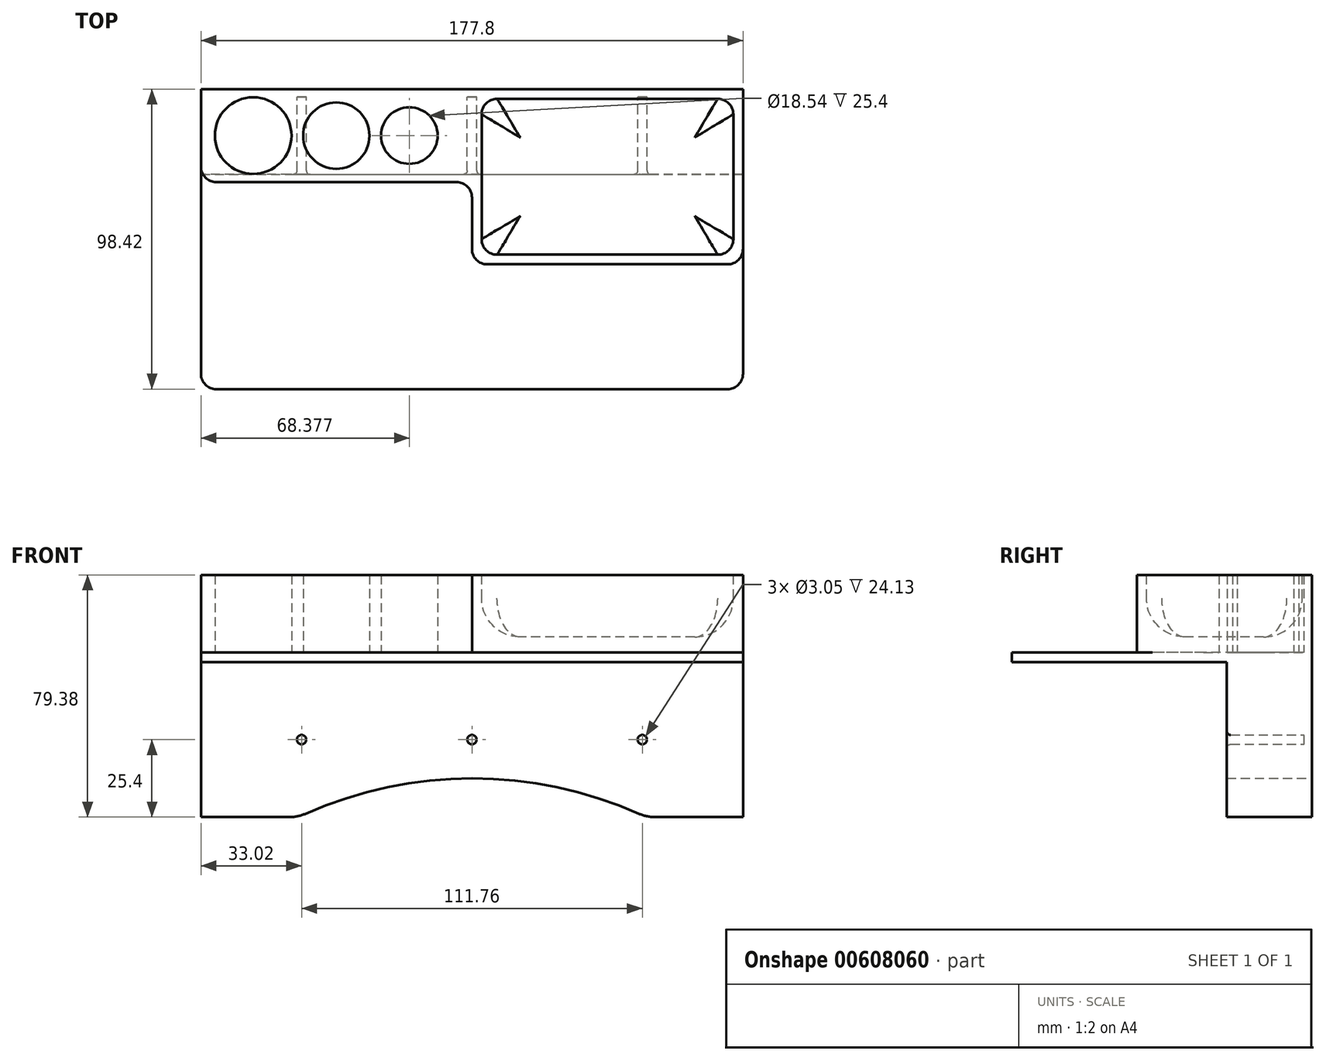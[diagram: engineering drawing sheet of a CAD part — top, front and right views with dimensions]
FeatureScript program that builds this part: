
annotation { "Feature Type Name" : "Feature", "Feature Type Description" : "" }
export const myFeature = defineFeature(function(context is Context, id is Id, definition is map)
    precondition{}
    {
        {
            var Q0;
            Q0=qCreatedBy(makeId("Top.planeOp"),FACE);
            var sketch = newSketch(context, id + "F0", { "sketchPlane" : qUnion([Q0])});
            skLineSegment(sketch, "E0.bottom", {"start": v(88.9, 47.62) * mm, "end": v(-88.9, 47.62) * mm});
            skLineSegment(sketch, "E0.top", {"start": v(88.9, -47.63) * mm, "end": v(-88.9, -47.63) * mm});
            skLineSegment(sketch, "E0.left", {"start": v(88.9, 47.62) * mm, "end": v(88.9, -47.63) * mm});
            skLineSegment(sketch, "E0.right", {"start": v(-88.9, 47.62) * mm, "end": v(-88.9, -47.63) * mm});
            skPoint(sketch, "E0.middle", {"position": v(0, 0) * mm});
            skLineSegment(sketch, "E1", {"start": v(-88.9, 47.62) * mm, "end": v(-88.9, 50.8) * mm});
            skLineSegment(sketch, "E2", {"start": v(-88.9, 50.8) * mm, "end": v(88.9, 50.8) * mm});
            skLineSegment(sketch, "E3", {"start": v(88.9, 50.8) * mm, "end": v(88.9, 47.62) * mm});
            skSolve(sketch);
        }
        {
            var Q0;
            Q0=makeQuery(id+"F0.imprint","IMPRINT",FACE,{"disambiguationData":[TD([[makeQuery(id+"F0.imprint","IMPRINT",EDGE,{"derivedFrom":sQuery(id+"F0.wireOp",EDGE,"E0.bottom")}),1.0]])]});
            var Q1;
            Q1=makeQuery(id+"F0.imprint","IMPRINT",FACE,{"disambiguationData":[TD([[makeQuery(id+"F0.imprint","IMPRINT",EDGE,{"derivedFrom":sQuery(id+"F0.wireOp",EDGE,"E0.bottom")}),-1.0]])]});
            extrude(context, id + "F1", {"entities" : qUnion([Q0, Q1]), "depth" : 3.17 * mm, "offsetDistance" : 25.4 * mm});
        }
        {
            var Q0;
            Q0=makeQuery(id+"F1.opExtrude","SWEPT_EDGE",EDGE,{"disambiguationData":[OSD([sQuery(id+"F0.wireOp",EDGE,"E0.top"),sQuery(id+"F0.wireOp",EDGE,"E0.right")])]});
            var Q1;
            Q1=makeQuery(id+"F1.opExtrude","SWEPT_EDGE",EDGE,{"disambiguationData":[OSD([sQuery(id+"F0.wireOp",EDGE,"E0.top"),sQuery(id+"F0.wireOp",EDGE,"E0.left")])]});
            fillet(context, id + "F2", {"entities" : qUnion([Q0, Q1]), "radius" : 5.08 * mm, "tangentPropagation" : true, "allowEdgeOverflow" : false});
        }
        {
            var Q0;
            Q0=makeQuery(id+"F1.opExtrude","CAP_FACE",FACE,{"disambiguationData":[OSD([sQuery(id+"F0.wireOp",EDGE,"E0.bottom"),sQuery(id+"F0.wireOp",EDGE,"E0.top"),sQuery(id+"F0.wireOp",EDGE,"E0.left"),sQuery(id+"F0.wireOp",EDGE,"E0.right")])],"isStart":false});
            var sketch = newSketch(context, id + "F3", { "sketchPlane" : qUnion([Q0])});
            skLineSegment(sketch, "E4.0", {"start": v(88.9, 47.62) * mm, "end": v(-88.9, 47.62) * mm});
            skLineSegment(sketch, "E5.0", {"start": v(88.9, 50.8) * mm, "end": v(-88.9, 50.8) * mm});
            skLineSegment(sketch, "E6.0", {"start": v(88.9, -3.18) * mm, "end": v(-88.9, -3.18) * mm});
            skLineSegment(sketch, "E7.0", {"start": v(88.9, -6.69) * mm, "end": v(-88.9, -6.69) * mm});
            skLineSegment(sketch, "E8", {"start": v(88.9, 50.8) * mm, "end": v(88.9, -6.69) * mm});
            skLineSegment(sketch, "E9", {"start": v(-88.9, 50.8) * mm, "end": v(-88.9, -6.69) * mm});
            skLineSegment(sketch, "E10", {"start": v(-88.9, 35.56) * mm, "end": v(88.9, 35.56) * mm});
            skCircle(sketch, "E11", {"center": v(-71.76, 35.56) * mm, "radius": 12.57 * mm});
            skCircle(sketch, "E12", {"center": v(-44.49, 35.56) * mm, "radius": 10.88 * mm});
            skCircle(sketch, "E13", {"center": v(-20.52, 35.56) * mm, "radius": 9.27 * mm});
            skLineSegment(sketch, "E14.0", {"start": v(-88.9, 20.32) * mm, "end": v(88.9, 20.32) * mm});
            skLineSegment(sketch, "E15", {"start": v(0, 50.8) * mm, "end": v(0, -6.69) * mm});
            skLineSegment(sketch, "E16.0", {"start": v(3.18, 50.8) * mm, "end": v(3.18, -6.69) * mm});
            skLineSegment(sketch, "E17.0", {"start": v(85.73, 50.8) * mm, "end": v(85.73, -6.69) * mm});
            skSolve(sketch);
        }
        {
            var Q0;
            {var subQ0=sQuery(id+"F3.wireOp",EDGE,"E9");var subQ1=sQuery(id+"F3.wireOp",EDGE,"E4.0");var subQ2=makeQuery(id+"F3.imprint","INTERSECT",VERTEX,{"derivedFrom":[subQ1,subQ0]});Q0=makeQuery(id+"F3.imprint","IMPRINT",FACE,{"disambiguationData":[TD([[makeQuery(id+"F3.imprint","IMPRINT",EDGE,{"disambiguationData":[TD([[subQ2,1.0]])],"derivedFrom":subQ1}),1.0]])]});}
            var Q1;
            {var subQ1=sQuery(id+"F3.wireOp",EDGE,"E4.0");var subQ5=sQuery(id+"F3.wireOp",EDGE,"E15");var subQ9=makeQuery(id+"F3.imprint","INTERSECT",VERTEX,{"derivedFrom":[subQ1,subQ5]});Q1=makeQuery(id+"F3.imprint","IMPRINT",FACE,{"disambiguationData":[TD([[makeQuery(id+"F3.imprint","IMPRINT",EDGE,{"disambiguationData":[TD([[subQ9,-1.0]])],"derivedFrom":subQ1}),-1.0]])]});}
            var Q2;
            {var subQ3=sQuery(id+"F3.wireOp",EDGE,"E15");var subQ11=sQuery(id+"F3.wireOp",EDGE,"E4.0");var subQ12=makeQuery(id+"F3.imprint","INTERSECT",VERTEX,{"derivedFrom":[subQ11,subQ3]});Q2=makeQuery(id+"F3.imprint","IMPRINT",FACE,{"disambiguationData":[TD([[makeQuery(id+"F3.imprint","IMPRINT",EDGE,{"disambiguationData":[TD([[subQ12,-1.0]])],"derivedFrom":subQ11}),1.0]])]});}
            var Q3;
            {var subQ1=sQuery(id+"F3.wireOp",EDGE,"E10");var subQ13=sQuery(id+"F3.wireOp",EDGE,"E9");var subQ14=makeQuery(id+"F3.imprint","INTERSECT",VERTEX,{"derivedFrom":[subQ13,subQ1]});Q3=makeQuery(id+"F3.imprint","IMPRINT",FACE,{"disambiguationData":[TD([[makeQuery(id+"F3.imprint","IMPRINT",EDGE,{"disambiguationData":[TD([[subQ14,-1.0]])],"derivedFrom":subQ13}),1.0]])]});}
            var Q4;
            {var subQ0=sQuery(id+"F3.wireOp",EDGE,"E16.0");var subQ1=sQuery(id+"F3.wireOp",EDGE,"E4.0");var subQ2=makeQuery(id+"F3.imprint","INTERSECT",VERTEX,{"derivedFrom":[subQ1,subQ0]});Q4=makeQuery(id+"F3.imprint","IMPRINT",FACE,{"disambiguationData":[TD([[makeQuery(id+"F3.imprint","IMPRINT",EDGE,{"disambiguationData":[TD([[subQ2,-1.0]])],"derivedFrom":subQ1}),-1.0]])]});}
            var Q5;
            {var subQ0=sQuery(id+"F3.wireOp",EDGE,"E16.0");var subQ1=sQuery(id+"F3.wireOp",EDGE,"E4.0");var subQ2=makeQuery(id+"F3.imprint","INTERSECT",VERTEX,{"derivedFrom":[subQ1,subQ0]});Q5=makeQuery(id+"F3.imprint","IMPRINT",FACE,{"disambiguationData":[TD([[makeQuery(id+"F3.imprint","IMPRINT",EDGE,{"disambiguationData":[TD([[subQ2,-1.0]])],"derivedFrom":subQ1}),1.0]])]});}
            var Q6;
            {var subQ0=sQuery(id+"F3.wireOp",EDGE,"E15");var subQ1=sQuery(id+"F3.wireOp",EDGE,"E10");var subQ2=makeQuery(id+"F3.imprint","INTERSECT",VERTEX,{"derivedFrom":[subQ1,subQ0]});Q6=makeQuery(id+"F3.imprint","IMPRINT",FACE,{"disambiguationData":[TD([[makeQuery(id+"F3.imprint","IMPRINT",EDGE,{"disambiguationData":[TD([[subQ2,-1.0]])],"derivedFrom":subQ1}),-1.0]])]});}
            var Q7;
            {var subQ0=sQuery(id+"F3.wireOp",EDGE,"E17.0");var subQ1=sQuery(id+"F3.wireOp",EDGE,"E4.0");var subQ2=makeQuery(id+"F3.imprint","INTERSECT",VERTEX,{"derivedFrom":[subQ1,subQ0]});Q7=makeQuery(id+"F3.imprint","IMPRINT",FACE,{"disambiguationData":[TD([[makeQuery(id+"F3.imprint","IMPRINT",EDGE,{"disambiguationData":[TD([[subQ2,-1.0]])],"derivedFrom":subQ1}),-1.0]])]});}
            var Q8;
            {var subQ0=sQuery(id+"F3.wireOp",EDGE,"E8");var subQ1=sQuery(id+"F3.wireOp",EDGE,"E4.0");var subQ2=makeQuery(id+"F3.imprint","INTERSECT",VERTEX,{"derivedFrom":[subQ1,subQ0]});Q8=makeQuery(id+"F3.imprint","IMPRINT",FACE,{"disambiguationData":[TD([[makeQuery(id+"F3.imprint","IMPRINT",EDGE,{"disambiguationData":[TD([[subQ2,-1.0]])],"derivedFrom":subQ1}),-1.0]])]});}
            var Q9;
            {var subQ0=sQuery(id+"F3.wireOp",EDGE,"E8");var subQ1=sQuery(id+"F3.wireOp",EDGE,"E4.0");var subQ2=makeQuery(id+"F3.imprint","INTERSECT",VERTEX,{"derivedFrom":[subQ1,subQ0]});Q9=makeQuery(id+"F3.imprint","IMPRINT",FACE,{"disambiguationData":[TD([[makeQuery(id+"F3.imprint","IMPRINT",EDGE,{"disambiguationData":[TD([[subQ2,-1.0]])],"derivedFrom":subQ1}),1.0]])]});}
            var Q10;
            {var subQ0=sQuery(id+"F3.wireOp",EDGE,"E10");var subQ1=sQuery(id+"F3.wireOp",EDGE,"E8");var subQ2=makeQuery(id+"F3.imprint","INTERSECT",VERTEX,{"derivedFrom":[subQ1,subQ0]});Q10=makeQuery(id+"F3.imprint","IMPRINT",FACE,{"disambiguationData":[TD([[makeQuery(id+"F3.imprint","IMPRINT",EDGE,{"disambiguationData":[TD([[subQ2,-1.0]])],"derivedFrom":subQ1}),-1.0]])]});}
            var Q11;
            {var subQ0=sQuery(id+"F3.wireOp",EDGE,"E17.0");var subQ1=sQuery(id+"F3.wireOp",EDGE,"E4.0");var subQ2=makeQuery(id+"F3.imprint","INTERSECT",VERTEX,{"derivedFrom":[subQ1,subQ0]});Q11=makeQuery(id+"F3.imprint","IMPRINT",FACE,{"disambiguationData":[TD([[makeQuery(id+"F3.imprint","IMPRINT",EDGE,{"disambiguationData":[TD([[subQ2,-1.0]])],"derivedFrom":subQ1}),1.0]])]});}
            var Q12;
            {var subQ0=sQuery(id+"F3.wireOp",EDGE,"E16.0");var subQ1=sQuery(id+"F3.wireOp",EDGE,"E10");var subQ2=makeQuery(id+"F3.imprint","INTERSECT",VERTEX,{"derivedFrom":[subQ1,subQ0]});Q12=makeQuery(id+"F3.imprint","IMPRINT",FACE,{"disambiguationData":[TD([[makeQuery(id+"F3.imprint","IMPRINT",EDGE,{"disambiguationData":[TD([[subQ2,-1.0]])],"derivedFrom":subQ1}),-1.0]])]});}
            var Q13;
            {var subQ0=sQuery(id+"F3.wireOp",EDGE,"E17.0");var subQ1=sQuery(id+"F3.wireOp",EDGE,"E6.0");var subQ2=makeQuery(id+"F3.imprint","INTERSECT",VERTEX,{"derivedFrom":[subQ1,subQ0]});Q13=makeQuery(id+"F3.imprint","IMPRINT",FACE,{"disambiguationData":[TD([[makeQuery(id+"F3.imprint","IMPRINT",EDGE,{"disambiguationData":[TD([[subQ2,-1.0]])],"derivedFrom":subQ1}),-1.0]])]});}
            var Q14;
            {var subQ0=sQuery(id+"F3.wireOp",EDGE,"E16.0");var subQ1=sQuery(id+"F3.wireOp",EDGE,"E6.0");var subQ2=makeQuery(id+"F3.imprint","INTERSECT",VERTEX,{"derivedFrom":[subQ1,subQ0]});Q14=makeQuery(id+"F3.imprint","IMPRINT",FACE,{"disambiguationData":[TD([[makeQuery(id+"F3.imprint","IMPRINT",EDGE,{"disambiguationData":[TD([[subQ2,-1.0]])],"derivedFrom":subQ1}),1.0]])]});}
            var Q15;
            {var subQ0=sQuery(id+"F3.wireOp",EDGE,"E17.0");var subQ1=sQuery(id+"F3.wireOp",EDGE,"E6.0");var subQ2=makeQuery(id+"F3.imprint","INTERSECT",VERTEX,{"derivedFrom":[subQ1,subQ0]});Q15=makeQuery(id+"F3.imprint","IMPRINT",FACE,{"disambiguationData":[TD([[makeQuery(id+"F3.imprint","IMPRINT",EDGE,{"disambiguationData":[TD([[subQ2,-1.0]])],"derivedFrom":subQ1}),1.0]])]});}
            var Q16;
            {var subQ0=sQuery(id+"F3.wireOp",EDGE,"E8");var subQ1=sQuery(id+"F3.wireOp",EDGE,"E6.0");var subQ2=makeQuery(id+"F3.imprint","INTERSECT",VERTEX,{"derivedFrom":[subQ1,subQ0]});Q16=makeQuery(id+"F3.imprint","IMPRINT",FACE,{"disambiguationData":[TD([[makeQuery(id+"F3.imprint","IMPRINT",EDGE,{"disambiguationData":[TD([[subQ2,-1.0]])],"derivedFrom":subQ1}),-1.0]])]});}
            var Q17;
            {var subQ0=sQuery(id+"F3.wireOp",EDGE,"E8");var subQ1=sQuery(id+"F3.wireOp",EDGE,"E6.0");var subQ2=makeQuery(id+"F3.imprint","INTERSECT",VERTEX,{"derivedFrom":[subQ1,subQ0]});Q17=makeQuery(id+"F3.imprint","IMPRINT",FACE,{"disambiguationData":[TD([[makeQuery(id+"F3.imprint","IMPRINT",EDGE,{"disambiguationData":[TD([[subQ2,-1.0]])],"derivedFrom":subQ1}),1.0]])]});}
            var Q18;
            {var subQ0=sQuery(id+"F3.wireOp",EDGE,"E16.0");var subQ1=sQuery(id+"F3.wireOp",EDGE,"E6.0");var subQ2=makeQuery(id+"F3.imprint","INTERSECT",VERTEX,{"derivedFrom":[subQ1,subQ0]});Q18=makeQuery(id+"F3.imprint","IMPRINT",FACE,{"disambiguationData":[TD([[makeQuery(id+"F3.imprint","IMPRINT",EDGE,{"disambiguationData":[TD([[subQ2,-1.0]])],"derivedFrom":subQ1}),-1.0]])]});}
            extrude(context, id + "F4", {"entities" : qUnion([Q0, Q1, Q2, Q3, Q4, Q5, Q6, Q7, Q8, Q9, Q10, Q11, Q12, Q13, Q14, Q15, Q16, Q17, Q18]), "operationType" : NewBodyOperationType.ADD, "depth" : 25.4 * mm, "offsetDistance" : 25.4 * mm});
        }
        {
            var Q0;
            Q0=makeQuery(id+"F4.opExtrude","CAP_FACE",FACE,{"disambiguationData":[OSD([sQuery(id+"F3.wireOp",EDGE,"E5.0"),sQuery(id+"F3.wireOp",EDGE,"E7.0"),sQuery(id+"F3.wireOp",EDGE,"E8"),sQuery(id+"F3.wireOp",EDGE,"E9"),sQuery(id+"F3.wireOp",EDGE,"E11"),sQuery(id+"F3.wireOp",EDGE,"E12"),sQuery(id+"F3.wireOp",EDGE,"E13"),sQuery(id+"F3.wireOp",EDGE,"E14.0"),sQuery(id+"F3.wireOp",EDGE,"E15")])],"isStart":false});
            var sketch = newSketch(context, id + "F5", { "sketchPlane" : qUnion([Q0])});
            skLineSegment(sketch, "E18.0", {"start": v(88.9, 50.8) * mm, "end": v(0, 50.8) * mm});
            skLineSegment(sketch, "E18.1", {"start": v(88.9, 50.8) * mm, "end": v(88.9, -6.69) * mm});
            skLineSegment(sketch, "E18.2", {"start": v(88.9, -6.69) * mm, "end": v(0, -6.69) * mm});
            skLineSegment(sketch, "E18.3", {"start": v(0, 50.8) * mm, "end": v(0, -6.69) * mm});
            skPoint(sketch, "E19.orphan", {"position": v(0, 20.32) * mm});
            skPoint(sketch, "E20.orphan", {"position": v(-88.9, 50.8) * mm});
            skLineSegment(sketch, "E21.0", {"start": v(85.73, 47.62) * mm, "end": v(3.17, 47.62) * mm});
            skLineSegment(sketch, "E21.1", {"start": v(85.73, 47.62) * mm, "end": v(85.73, -3.51) * mm});
            skLineSegment(sketch, "E21.2", {"start": v(85.73, -3.51) * mm, "end": v(3.17, -3.51) * mm});
            skLineSegment(sketch, "E21.3", {"start": v(3.17, 47.62) * mm, "end": v(3.17, -3.51) * mm});
            skSolve(sketch);
        }
        {
            var Q0;
            Q0=makeQuery(id+"F5.imprint","IMPRINT",FACE,{"disambiguationData":[TD([[makeQuery(id+"F5.imprint","IMPRINT",EDGE,{"derivedFrom":sQuery(id+"F5.wireOp",EDGE,"E21.0")}),1.0]])]});
            extrude(context, id + "F6", {"entities" : qUnion([Q0]), "operationType" : NewBodyOperationType.REMOVE, "depth" : -20.32 * mm, "offsetDistance" : 25.4 * mm});
        }
        {
            var Q0;
            Q0=makeQuery(id+"F6.boolean.opBoolean","COPY",EDGE,{"derivedFrom":makeQuery(id+"F6.opExtrude","CAP_EDGE",EDGE,{"disambiguationData":[OSD([sQuery(id+"F5.wireOp",EDGE,"E21.0")])],"isStart":false})});
            var Q1;
            Q1=makeQuery(id+"F6.boolean.opBoolean","COPY",EDGE,{"derivedFrom":makeQuery(id+"F6.opExtrude","CAP_EDGE",EDGE,{"disambiguationData":[OSD([sQuery(id+"F5.wireOp",EDGE,"E21.1")])],"isStart":false})});
            var Q2;
            Q2=makeQuery(id+"F6.boolean.opBoolean","COPY",EDGE,{"derivedFrom":makeQuery(id+"F6.opExtrude","CAP_EDGE",EDGE,{"disambiguationData":[OSD([sQuery(id+"F5.wireOp",EDGE,"E21.2")])],"isStart":false})});
            var Q3;
            Q3=makeQuery(id+"F6.boolean.opBoolean","COPY",EDGE,{"derivedFrom":makeQuery(id+"F6.opExtrude","CAP_EDGE",EDGE,{"disambiguationData":[OSD([sQuery(id+"F5.wireOp",EDGE,"E21.3")])],"isStart":false})});
            fillet(context, id + "F7", {"entities" : qUnion([Q0, Q1, Q2, Q3]), "radius" : 12.7 * mm, "tangentPropagation" : true, "allowEdgeOverflow" : false});
        }
        {
            var Q0;
            Q0=makeQuery(id+"F6.boolean.opBoolean","COPY",EDGE,{"derivedFrom":makeQuery(id+"F6.opExtrude","SWEPT_EDGE",EDGE,{"disambiguationData":[OSD([sQuery(id+"F5.wireOp",EDGE,"E21.0"),sQuery(id+"F5.wireOp",EDGE,"E21.1")])]})});
            var Q1;
            Q1=makeQuery(id+"F6.boolean.opBoolean","COPY",EDGE,{"derivedFrom":makeQuery(id+"F6.opExtrude","SWEPT_EDGE",EDGE,{"disambiguationData":[OSD([sQuery(id+"F5.wireOp",EDGE,"E21.1"),sQuery(id+"F5.wireOp",EDGE,"E21.2")])]})});
            var Q2;
            Q2=makeQuery(id+"F6.boolean.opBoolean","COPY",EDGE,{"derivedFrom":makeQuery(id+"F6.opExtrude","SWEPT_EDGE",EDGE,{"disambiguationData":[OSD([sQuery(id+"F5.wireOp",EDGE,"E21.0"),sQuery(id+"F5.wireOp",EDGE,"E21.3")])]})});
            var Q3;
            Q3=makeQuery(id+"F6.boolean.opBoolean","COPY",EDGE,{"derivedFrom":makeQuery(id+"F6.opExtrude","SWEPT_EDGE",EDGE,{"disambiguationData":[OSD([sQuery(id+"F5.wireOp",EDGE,"E21.2"),sQuery(id+"F5.wireOp",EDGE,"E21.3")])]})});
            fillet(context, id + "F8", {"entities" : qUnion([Q0, Q1, Q2, Q3]), "radius" : 5.08 * mm, "tangentPropagation" : true, "allowEdgeOverflow" : false});
        }
        {
            var Q0;
            Q0=makeQuery(id+"F4.opExtrude","SWEPT_EDGE",EDGE,{"disambiguationData":[OSD([sQuery(id+"F3.wireOp",EDGE,"E7.0"),sQuery(id+"F3.wireOp",EDGE,"E15")])]});
            var Q1;
            Q1=makeQuery(id+"F4.opExtrude","SWEPT_EDGE",EDGE,{"disambiguationData":[OSD([sQuery(id+"F3.wireOp",EDGE,"E14.0"),sQuery(id+"F3.wireOp",EDGE,"E15")])]});
            var Q2;
            Q2=makeQuery(id+"F4.opExtrude","SWEPT_EDGE",EDGE,{"disambiguationData":[OSD([sQuery(id+"F3.wireOp",EDGE,"E9"),sQuery(id+"F3.wireOp",EDGE,"E14.0")])]});
            var Q3;
            Q3=makeQuery(id+"F4.opExtrude","SWEPT_EDGE",EDGE,{"disambiguationData":[OSD([sQuery(id+"F0.wireOp",EDGE,"E0.left"),sQuery(id+"F0.wireOp",EDGE,"E3"),sQuery(id+"F3.wireOp",EDGE,"E7.0"),sQuery(id+"F3.wireOp",EDGE,"E8")])]});
            fillet(context, id + "F9", {"entities" : qUnion([Q0, Q1, Q2, Q3]), "radius" : 5.08 * mm, "tangentPropagation" : true, "allowEdgeOverflow" : false});
        }
        {
            var Q0;
            Q0=makeQuery(id+"F4.boolean.opBoolean","MERGE",FACE,{"derivedFrom":[makeQuery(id+"F1.opExtrude","SWEPT_FACE",FACE,{"disambiguationData":[OSD([sQuery(id+"F0.wireOp",EDGE,"E2")])]}),makeQuery(id+"F4.opExtrude","SWEPT_FACE",FACE,{"disambiguationData":[OSD([sQuery(id+"F3.wireOp",EDGE,"E5.0")])]})]});
            var sketch = newSketch(context, id + "F10", { "sketchPlane" : qUnion([Q0])});
            skLineSegment(sketch, "E22", {"start": v(-88.9, 0) * mm, "end": v(-88.9, -50.8) * mm});
            skLineSegment(sketch, "E23", {"start": v(-88.9, -50.8) * mm, "end": v(88.9, -50.8) * mm});
            skLineSegment(sketch, "E24", {"start": v(88.9, -50.8) * mm, "end": v(88.9, 0) * mm});
            skLineSegment(sketch, "E25.0", {"start": v(-57.15, 0) * mm, "end": v(-57.15, -50.8) * mm});
            skLineSegment(sketch, "E26.0", {"start": v(57.15, -50.9) * mm, "end": v(57.15, 0) * mm});
            skLineSegment(sketch, "E27.0", {"start": v(-88.9, -38.1) * mm, "end": v(88.9, -38.1) * mm});
            skArc(sketch, "E28", {"start": v(57.15, -50.9) * mm, "mid": v(0.01, -38.1) * mm, "end": v(-57.15, -50.8) * mm});
            skSolve(sketch);
        }
        {
            var Q0;
            {var subQ1=sQuery(id+"F0.wireOp",EDGE,"E2");var subQ2=makeQuery(id+"F1.opExtrude","CAP_EDGE",EDGE,{"disambiguationData":[OSD([subQ1])],"isStart":true});var subQ6=sQuery(id+"F10.wireOp",EDGE,"E25.0");var subQ7=makeQuery(id+"F10.imprint","INTERSECT",VERTEX,{"derivedFrom":[subQ2,subQ6]});Q0=makeQuery(id+"F10.imprint","IMPRINT",FACE,{"disambiguationData":[TD([[makeQuery(id+"F10.imprint","IMPRINT",EDGE,{"disambiguationData":[TD([[subQ7,-1.0]])],"derivedFrom":subQ6}),-1.0]])]});}
            var Q1;
            {var subQ0=sQuery(id+"F10.wireOp",EDGE,"E23");var subQ1=sQuery(id+"F10.wireOp",EDGE,"E22");var subQ2=makeQuery(id+"F10.imprint","INTERSECT",VERTEX,{"derivedFrom":[subQ1,subQ0]});Q1=makeQuery(id+"F10.imprint","IMPRINT",FACE,{"disambiguationData":[TD([[makeQuery(id+"F10.imprint","IMPRINT",EDGE,{"disambiguationData":[TD([[subQ2,1.0]])],"derivedFrom":subQ1}),1.0]])]});}
            var Q2;
            {var subQ1=sQuery(id+"F10.wireOp",EDGE,"E25.0");var subQ3=sQuery(id+"F10.wireOp",EDGE,"E27.0");var subQ4=makeQuery(id+"F10.imprint","INTERSECT",VERTEX,{"derivedFrom":[subQ1,subQ3]});Q2=makeQuery(id+"F10.imprint","IMPRINT",FACE,{"disambiguationData":[TD([[makeQuery(id+"F10.imprint","IMPRINT",EDGE,{"disambiguationData":[TD([[subQ4,-1.0]])],"derivedFrom":subQ3}),-1.0]])]});}
            var Q3;
            {var subQ4=sQuery(id+"F10.wireOp",EDGE,"E25.0");var subQ6=makeQuery(id+"F1.opExtrude","CAP_EDGE",EDGE,{"disambiguationData":[OSD([sQuery(id+"F0.wireOp",EDGE,"E2")])],"isStart":true});var subQ7=makeQuery(id+"F10.imprint","INTERSECT",VERTEX,{"derivedFrom":[subQ6,subQ4]});Q3=makeQuery(id+"F10.imprint","IMPRINT",FACE,{"disambiguationData":[TD([[makeQuery(id+"F10.imprint","IMPRINT",EDGE,{"disambiguationData":[TD([[subQ7,-1.0]])],"derivedFrom":subQ4}),1.0]])]});}
            var Q4;
            {var subQ0=sQuery(id+"F10.wireOp",EDGE,"E28");var subQ1=sQuery(id+"F10.wireOp",EDGE,"E23");var subQ2=makeQuery(id+"F10.imprint","INTERSECT",VERTEX,{"derivedFrom":[subQ1,subQ0]});Q4=makeQuery(id+"F10.imprint","IMPRINT",FACE,{"disambiguationData":[TD([[makeQuery(id+"F10.imprint","IMPRINT",EDGE,{"disambiguationData":[TD([[subQ2,-1.0]])],"derivedFrom":subQ1}),1.0]])]});}
            var Q5;
            {var subQ1=sQuery(id+"F0.wireOp",EDGE,"E2");var subQ2=makeQuery(id+"F1.opExtrude","CAP_EDGE",EDGE,{"disambiguationData":[OSD([subQ1])],"isStart":true});var subQ6=sQuery(id+"F10.wireOp",EDGE,"E26.0");var subQ7=makeQuery(id+"F10.imprint","INTERSECT",VERTEX,{"derivedFrom":[subQ2,subQ6]});Q5=makeQuery(id+"F10.imprint","IMPRINT",FACE,{"disambiguationData":[TD([[makeQuery(id+"F10.imprint","IMPRINT",EDGE,{"disambiguationData":[TD([[subQ7,1.0]])],"derivedFrom":subQ6}),-1.0]])]});}
            var Q6;
            {var subQ0=sQuery(id+"F10.wireOp",EDGE,"E24");var subQ1=sQuery(id+"F10.wireOp",EDGE,"E23");var subQ2=makeQuery(id+"F10.imprint","INTERSECT",VERTEX,{"derivedFrom":[subQ1,subQ0]});Q6=makeQuery(id+"F10.imprint","IMPRINT",FACE,{"disambiguationData":[TD([[makeQuery(id+"F10.imprint","IMPRINT",EDGE,{"disambiguationData":[TD([[subQ2,1.0]])],"derivedFrom":subQ1}),1.0]])]});}
            extrude(context, id + "F11", {"entities" : qUnion([Q0, Q1, Q2, Q3, Q4, Q5, Q6]), "operationType" : NewBodyOperationType.ADD, "oppositeDirection" : true, "depth" : 2.54 * mm, "offsetDistance" : 25.4 * mm});
        }
        {
            var Q0;
            Q0=makeQuery(id+"F11.opExtrude","SWEPT_EDGE",EDGE,{"disambiguationData":[OSD([sQuery(id+"F10.wireOp",EDGE,"E23"),sQuery(id+"F10.wireOp",EDGE,"E28")])]});
            var Q1;
            Q1=makeQuery(id+"F11.opExtrude","SWEPT_EDGE",EDGE,{"disambiguationData":[OSD([sQuery(id+"F10.wireOp",EDGE,"E23"),sQuery(id+"F10.wireOp",EDGE,"E25.0"),sQuery(id+"F10.wireOp",EDGE,"E28")])]});
            fillet(context, id + "F12", {"entities" : qUnion([Q0, Q1]), "radius" : 12.7 * mm, "tangentPropagation" : true, "allowEdgeOverflow" : false});
        }
        {
            var Q0;
            Q0=makeQuery(id+"F11.opExtrude","CAP_FACE",FACE,{"disambiguationData":[OSD([sQuery(id+"F0.wireOp",EDGE,"E2"),sQuery(id+"F10.wireOp",EDGE,"E22"),sQuery(id+"F10.wireOp",EDGE,"E23"),sQuery(id+"F10.wireOp",EDGE,"E24"),sQuery(id+"F10.wireOp",EDGE,"E28")])],"isStart":false});
            var sketch = newSketch(context, id + "F13", { "sketchPlane" : qUnion([Q0])});
            skLineSegment(sketch, "E29", {"start": v(-88.9, -25.4) * mm, "end": v(88.9, -25.4) * mm});
            skCircle(sketch, "E30", {"center": v(-55.88, -25.4) * mm, "radius": 1.52 * mm});
            skCircle(sketch, "E31", {"center": v(-27.94, -25.4) * mm, "radius": 1.52 * mm});
            skCircle(sketch, "E32", {"center": v(0, -25.4) * mm, "radius": 1.52 * mm});
            skCircle(sketch, "E33", {"center": v(27.94, -25.4) * mm, "radius": 1.52 * mm});
            skCircle(sketch, "E34", {"center": v(55.88, -25.4) * mm, "radius": 1.52 * mm});
            skSolve(sketch);
        }
        {
            var Q0;
            {var subQ0=sQuery(id+"F13.wireOp",EDGE,"E30");var subQ1=sQuery(id+"F13.wireOp",EDGE,"E29");var subQ2=makeQuery(id+"F13.imprint","INTERSECT",VERTEX,{"disambiguationData":[OD(0.0)],"derivedFrom":[subQ1,subQ0]});Q0=makeQuery(id+"F13.imprint","IMPRINT",FACE,{"disambiguationData":[TD([[makeQuery(id+"F13.imprint","IMPRINT",EDGE,{"disambiguationData":[TD([[subQ2,-1.0]])],"derivedFrom":subQ1}),-1.0]])]});}
            var Q1;
            {var subQ0=sQuery(id+"F13.wireOp",EDGE,"E30");var subQ1=sQuery(id+"F13.wireOp",EDGE,"E29");var subQ2=makeQuery(id+"F13.imprint","INTERSECT",VERTEX,{"disambiguationData":[OD(0.0)],"derivedFrom":[subQ1,subQ0]});Q1=makeQuery(id+"F13.imprint","IMPRINT",FACE,{"disambiguationData":[TD([[makeQuery(id+"F13.imprint","IMPRINT",EDGE,{"disambiguationData":[TD([[subQ2,-1.0]])],"derivedFrom":subQ1}),1.0]])]});}
            var Q2;
            {var subQ0=sQuery(id+"F13.wireOp",EDGE,"E31");var subQ1=sQuery(id+"F13.wireOp",EDGE,"E29");var subQ2=makeQuery(id+"F13.imprint","INTERSECT",VERTEX,{"disambiguationData":[OD(0.0)],"derivedFrom":[subQ1,subQ0]});Q2=makeQuery(id+"F13.imprint","IMPRINT",FACE,{"disambiguationData":[TD([[makeQuery(id+"F13.imprint","IMPRINT",EDGE,{"disambiguationData":[TD([[subQ2,-1.0]])],"derivedFrom":subQ1}),1.0]])]});}
            var Q3;
            {var subQ0=sQuery(id+"F13.wireOp",EDGE,"E31");var subQ1=sQuery(id+"F13.wireOp",EDGE,"E29");var subQ2=makeQuery(id+"F13.imprint","INTERSECT",VERTEX,{"disambiguationData":[OD(0.0)],"derivedFrom":[subQ1,subQ0]});Q3=makeQuery(id+"F13.imprint","IMPRINT",FACE,{"disambiguationData":[TD([[makeQuery(id+"F13.imprint","IMPRINT",EDGE,{"disambiguationData":[TD([[subQ2,-1.0]])],"derivedFrom":subQ1}),-1.0]])]});}
            var Q4;
            {var subQ0=sQuery(id+"F13.wireOp",EDGE,"E32");var subQ1=sQuery(id+"F13.wireOp",EDGE,"E29");var subQ2=makeQuery(id+"F13.imprint","INTERSECT",VERTEX,{"disambiguationData":[OD(0.0)],"derivedFrom":[subQ1,subQ0]});Q4=makeQuery(id+"F13.imprint","IMPRINT",FACE,{"disambiguationData":[TD([[makeQuery(id+"F13.imprint","IMPRINT",EDGE,{"disambiguationData":[TD([[subQ2,-1.0]])],"derivedFrom":subQ1}),1.0]])]});}
            var Q5;
            {var subQ0=sQuery(id+"F13.wireOp",EDGE,"E32");var subQ1=sQuery(id+"F13.wireOp",EDGE,"E29");var subQ2=makeQuery(id+"F13.imprint","INTERSECT",VERTEX,{"disambiguationData":[OD(0.0)],"derivedFrom":[subQ1,subQ0]});Q5=makeQuery(id+"F13.imprint","IMPRINT",FACE,{"disambiguationData":[TD([[makeQuery(id+"F13.imprint","IMPRINT",EDGE,{"disambiguationData":[TD([[subQ2,-1.0]])],"derivedFrom":subQ1}),-1.0]])]});}
            var Q6;
            {var subQ0=sQuery(id+"F13.wireOp",EDGE,"E33");var subQ1=sQuery(id+"F13.wireOp",EDGE,"E29");var subQ2=makeQuery(id+"F13.imprint","INTERSECT",VERTEX,{"disambiguationData":[OD(0.0)],"derivedFrom":[subQ1,subQ0]});Q6=makeQuery(id+"F13.imprint","IMPRINT",FACE,{"disambiguationData":[TD([[makeQuery(id+"F13.imprint","IMPRINT",EDGE,{"disambiguationData":[TD([[subQ2,-1.0]])],"derivedFrom":subQ1}),1.0]])]});}
            var Q7;
            {var subQ0=sQuery(id+"F13.wireOp",EDGE,"E33");var subQ1=sQuery(id+"F13.wireOp",EDGE,"E29");var subQ2=makeQuery(id+"F13.imprint","INTERSECT",VERTEX,{"disambiguationData":[OD(0.0)],"derivedFrom":[subQ1,subQ0]});Q7=makeQuery(id+"F13.imprint","IMPRINT",FACE,{"disambiguationData":[TD([[makeQuery(id+"F13.imprint","IMPRINT",EDGE,{"disambiguationData":[TD([[subQ2,-1.0]])],"derivedFrom":subQ1}),-1.0]])]});}
            var Q8;
            {var subQ0=sQuery(id+"F13.wireOp",EDGE,"E34");var subQ1=sQuery(id+"F13.wireOp",EDGE,"E29");var subQ2=makeQuery(id+"F13.imprint","INTERSECT",VERTEX,{"disambiguationData":[OD(0.0)],"derivedFrom":[subQ1,subQ0]});Q8=makeQuery(id+"F13.imprint","IMPRINT",FACE,{"disambiguationData":[TD([[makeQuery(id+"F13.imprint","IMPRINT",EDGE,{"disambiguationData":[TD([[subQ2,-1.0]])],"derivedFrom":subQ1}),1.0]])]});}
            var Q9;
            {var subQ0=sQuery(id+"F13.wireOp",EDGE,"E34");var subQ1=sQuery(id+"F13.wireOp",EDGE,"E29");var subQ2=makeQuery(id+"F13.imprint","INTERSECT",VERTEX,{"disambiguationData":[OD(0.0)],"derivedFrom":[subQ1,subQ0]});Q9=makeQuery(id+"F13.imprint","IMPRINT",FACE,{"disambiguationData":[TD([[makeQuery(id+"F13.imprint","IMPRINT",EDGE,{"disambiguationData":[TD([[subQ2,-1.0]])],"derivedFrom":subQ1}),-1.0]])]});}
            extrude(context, id + "F14", {"entities" : qUnion([Q0, Q1, Q2, Q3, Q4, Q5, Q6, Q7, Q8, Q9]), "operationType" : NewBodyOperationType.ADD, "depth" : 25.4 * mm, "offsetDistance" : 25.4 * mm});
        }
        {
            var Q0;
            Q0=makeQuery(id+"F14.opExtrude","CAP_EDGE",EDGE,{"disambiguationData":[OSD([sQuery(id+"F13.wireOp",EDGE,"E30")])],"isStart":false});
            var Q1;
            Q1=makeQuery(id+"F14.opExtrude","CAP_EDGE",EDGE,{"disambiguationData":[OSD([sQuery(id+"F13.wireOp",EDGE,"E31")])],"isStart":false});
            var Q2;
            Q2=makeQuery(id+"F14.opExtrude","CAP_EDGE",EDGE,{"disambiguationData":[OSD([sQuery(id+"F13.wireOp",EDGE,"E32")])],"isStart":false});
            var Q3;
            Q3=makeQuery(id+"F14.opExtrude","CAP_EDGE",EDGE,{"disambiguationData":[OSD([sQuery(id+"F13.wireOp",EDGE,"E33")])],"isStart":false});
            var Q4;
            Q4=makeQuery(id+"F14.opExtrude","CAP_EDGE",EDGE,{"disambiguationData":[OSD([sQuery(id+"F13.wireOp",EDGE,"E34")])],"isStart":false});
            fillet(context, id + "F15", {"entities" : qUnion([Q0, Q1, Q2, Q3, Q4]), "radius" : 1.27 * mm, "tangentPropagation" : true, "allowEdgeOverflow" : false});
        }
    });
